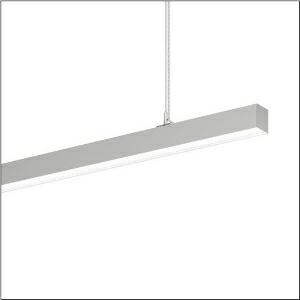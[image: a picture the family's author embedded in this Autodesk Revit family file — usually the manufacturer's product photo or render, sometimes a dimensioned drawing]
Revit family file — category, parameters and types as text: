
# Revit family: silica_r__21_51mx33tbt9s_9dae
name_source: partatom
category: Lighting Fixtures
units: mm (PartAtom-declared; Revit-internal decimal feet)

## family parameters
Cut with Voids When Loaded = No
Host = Face
Light Source = No
Part Type = Normal
Room Calculation Point = No
Round Connector Dimension = Use Diameter
Shared = No

## types (1)
- --- (1 x LED, 7170 lm, 67.4 W, 6500K)
    Apparent Load = 67 VA
    CIE Flux Codes = 78 96 99 56 100
    Color Rendering = 80
    Color Temperature = 6500K
    Default Elevation = 1800 mm
    Description = Silica® 21, office luminaire, primary optical cover: prismatic diffuser, of PMMA, CAT 2 (L<= 3000cd/m²), light emission: direct/indirect distribution, primary light characteristic: symmetric, installation type: suspended mounting, LED, rated luminous flux: 7.170lm, luminous efficacy: 101lm/W, light colour: 8tw, colour temperature: 2700..6500K, control gear: DALI DT8, with terminal, 3+2-pole, max. 2.5mm², mains connection: 220..240V, AC, 50/60Hz, rated input power: 70.8W, luminaire housing, of aluminium, metallic grey (RAL 9006), length: 1.504mm, width: 53mm, height: 53mm, protection rating (complete): IP20, insulation class (complete): insulation class I (protective earthing), certification: CE, permissible operating ambient temperature: 0..+35°C, standard: EN 50419, packaging unit: 1 piece
    Height = 53 mm
    Lamp = 1 x LED
    Lamp Light Flux = 7170 lm
    Lamp Power = 67.4 W
    Lamp count = 1
    Length = 1504 mm
    Luminous efficacy = 106 lm/W
    Manufacturer = Siteco
    ModVariant = No
    Model = 51MX33TBT9S
    Mounting Place = Ceiling
    Mounting Type = Pendant
    Number of Poles = 1
    OnlyDefault = Yes
    Power Factor = 1
    Product Name = Silica® 21
    Product group = office luminaire | ceiling pendant
    ProductGroupID = 904
    Protection Class = Protection class I
    Protection Degree = IP 20
    RLX_Detail_Level = 1
    RLX_Emergency_Light_Flux = 0 lm
    RLX_Emergency_Type = 0
    RLX_Emergency_Type_DB = No
    RlxData = <blob elided: 20209 chars, md5=44db20a3>
    Socket = socket
    Standby Power = 0 W
    System Light Flux = 7170 lm
    System Power = 67 W
    Type Comments = individual setting
    Type Image = l_1335864.jpg
    URL = http://relux.com
    VarID = @adj_139740
    Voltage = 0 V
    Weight = 0.00 kg
    Width = 53 mm

## geometry (parser evidence)
native form markers: Blend x4, Sweep x11
no freeform markers — native parametric forms only
